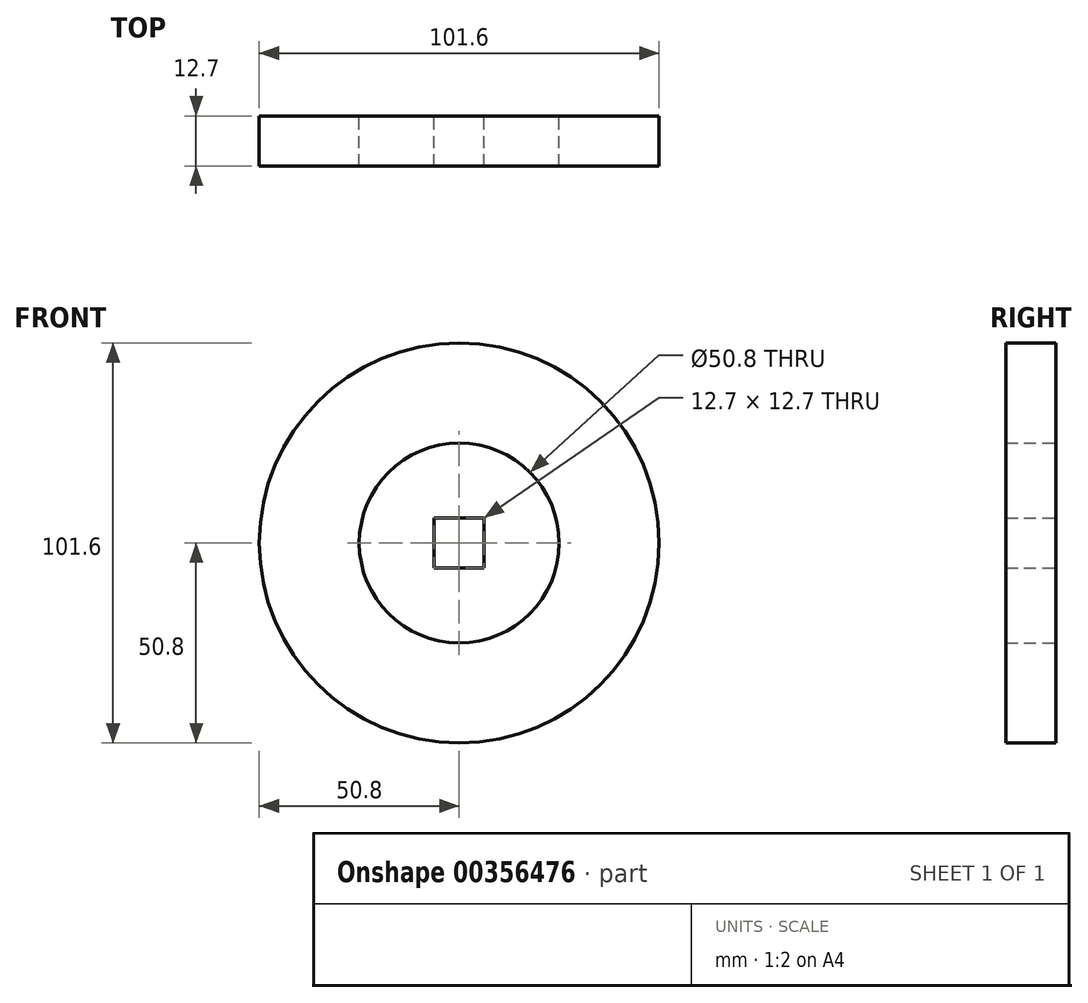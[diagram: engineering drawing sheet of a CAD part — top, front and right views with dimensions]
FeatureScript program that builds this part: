
annotation { "Feature Type Name" : "Feature", "Feature Type Description" : "" }
export const myFeature = defineFeature(function(context is Context, id is Id, definition is map)
    precondition{}
    {
        {
            var Q0;
            Q0=qCreatedBy(makeId("Front.planeOp"),FACE);
            var sketch = newSketch(context, id + "F0", { "sketchPlane" : qUnion([Q0])});
            skCircle(sketch, "E0", {"center": v(0, 0) * mm, "radius": 50.8 * mm});
            skCircle(sketch, "E1", {"center": v(0, 0) * mm, "radius": 25.4 * mm});
            skLineSegment(sketch, "E2.bottom", {"start": v(6.35, 6.35) * mm, "end": v(-6.35, 6.35) * mm});
            skLineSegment(sketch, "E2.top", {"start": v(6.35, -6.35) * mm, "end": v(-6.35, -6.35) * mm});
            skLineSegment(sketch, "E2.left", {"start": v(6.35, 6.35) * mm, "end": v(6.35, -6.35) * mm});
            skLineSegment(sketch, "E2.right", {"start": v(-6.35, 6.35) * mm, "end": v(-6.35, -6.35) * mm});
            skSolve(sketch);
        }
        {
            var Q0;
            Q0=makeQuery(id+"F0.imprint","IMPRINT",FACE,{"disambiguationData":[TD([[makeQuery(id+"F0.imprint","IMPRINT",EDGE,{"derivedFrom":sQuery(id+"F0.wireOp",EDGE,"E0")}),1.0]])]});
            extrude(context, id + "F1", {"entities" : qUnion([Q0]), "depth" : 12.7 * mm});
        }
        {
            var Q0;
            Q0=makeQuery(id+"F0.imprint","IMPRINT",FACE,{"disambiguationData":[TD([[makeQuery(id+"F0.imprint","IMPRINT",EDGE,{"derivedFrom":sQuery(id+"F0.wireOp",EDGE,"E1")}),1.0]])]});
            extrude(context, id + "F2", {"entities" : qUnion([Q0]), "depth" : 12.7 * mm});
        }
    });
